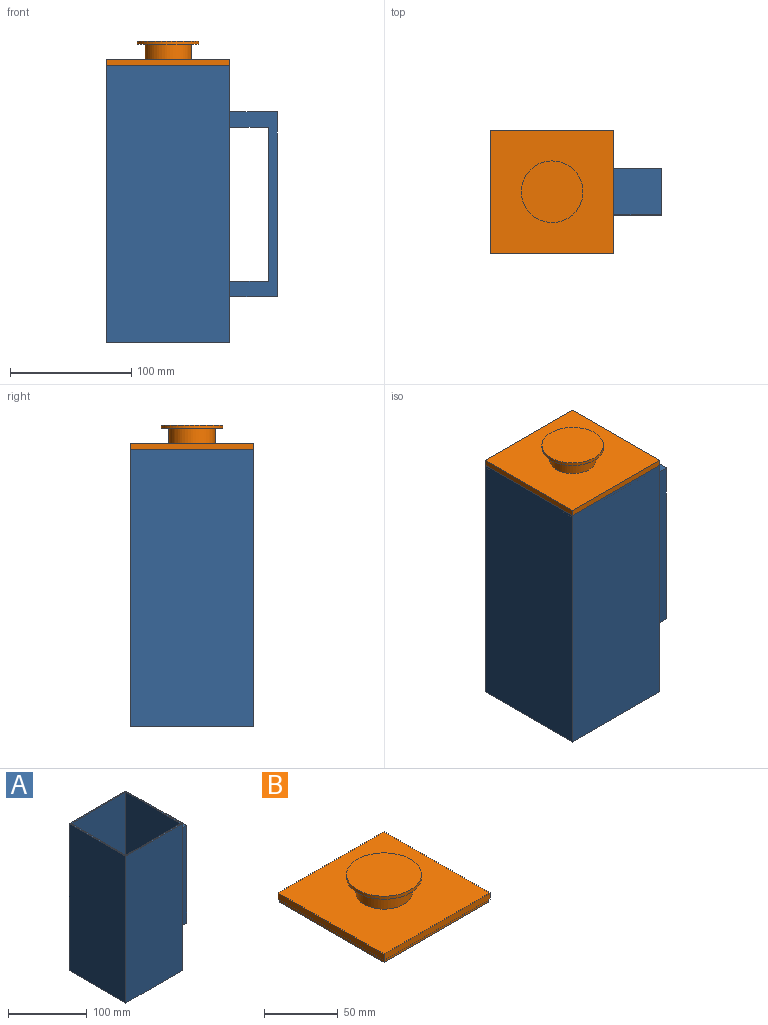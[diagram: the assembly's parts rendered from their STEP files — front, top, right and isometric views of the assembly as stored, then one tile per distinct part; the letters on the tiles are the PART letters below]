
ASSEMBLY  parts=2 mates=1
PART A: 19 faces, bbox 141x101.6x228.6 mm
  f0: plane 101.6x101.6mm, normal (0,0,1), area 635.1mm2, adj f1,f2,f3,f4,f14,f15,f16,f17
  f1: plane 228.6x101.6mm, normal (1,0,0), area 22258mm2, adj f0,f2,f4,f5,f6,f7,f8,f9
  f2: plane 228.6x101.6mm, normal (0,1,0), area 23225.8mm2, adj f0,f1,f3,f5
  f3: plane 228.6x101.6mm, normal (-1,0,0), area 23225.8mm2, adj f0,f2,f4,f5
  f4: plane 228.6x101.6mm, normal (0,-1,0), area 23225.8mm2, adj f0,f1,f3,f5
  f5: plane 101.6x101.6mm, normal (0,0,-1), area 10322.6mm2, adj f1,f2,f3,f4
  f6: plane 152.4x39.37mm, normal (0,1,0), area 1967.7mm2, adj f1,f7,f9,f10,f11,f12,f13
  f7: plane 39.37x38.1mm, normal (0,0,1), area 1500mm2, adj f1,f6,f8,f13
  f8: plane 152.4x39.37mm, normal (0,-1,0), area 1967.7mm2, adj f1,f7,f9,f10,f11,f12,f13
  f9: plane 38.1x31.75mm, normal (0,0,-1), area 1209.7mm2, adj f1,f6,f8,f12
  f10: plane 38.1x31.75mm, normal (0,0,1), area 1209.7mm2, adj f1,f6,f8,f12
  f11: plane 39.37x38.1mm, normal (0,0,-1), area 1500mm2, adj f1,f6,f8,f13
  f12: plane 127x38.1mm, normal (-1,0,0), area 4838.7mm2, adj f6,f8,f9,f10
  f13: plane 152.4x38.1mm, normal (1,0,0), area 5806.4mm2, adj f6,f7,f8,f11
  f14: plane 227.01x98.43mm, normal (0,-1,0), area 22343.7mm2, adj f0,f15,f17,f18
  f15: plane 227.01x98.43mm, normal (1,0,0), area 22343.7mm2, adj f0,f14,f16,f18
  f16: plane 227.01x98.43mm, normal (0,1,0), area 22343.7mm2, adj f0,f15,f17,f18
  f17: plane 227.01x98.43mm, normal (-1,0,0), area 22343.7mm2, adj f0,f14,f16,f18
  f18: plane 98.43x98.43mm, normal (0,0,1), area 9687.5mm2, adj f14,f15,f16,f17
PART B: 15 faces, bbox 101.6x101.6x22.9 mm
  f0: plane 100.01x2.54mm, normal (-1,0,0), area 254mm2, adj f1,f3,f4,f10
  f1: plane 100.01x2.54mm, normal (0,-1,0), area 254mm2, adj f0,f2,f4,f10
  f2: plane 100.01x2.54mm, normal (1,0,0), area 254mm2, adj f1,f3,f4,f10
  f3: plane 100.01x2.54mm, normal (0,1,0), area 254mm2, adj f0,f2,f4,f10
  f4: plane 100.01x100.01mm, normal (0,0,-1), area 10002.5mm2, adj f0,f1,f2,f3
  f5: plane 101.6x5.08mm, normal (0,1,0), area 516.1mm2, adj f6,f8,f9,f10
  f6: plane 101.6x5.08mm, normal (-1,0,0), area 516.1mm2, adj f5,f7,f9,f10
  f7: plane 101.6x5.08mm, normal (0,-1,0), area 516.1mm2, adj f6,f8,f9,f10
  f8: plane 101.6x5.08mm, normal (1,0,0), area 516.1mm2, adj f5,f7,f9,f10
  f9: plane 101.6x101.6mm, normal (0,0,1), area 9182.5mm2, adj f5,f6,f7,f8,f11
  f10: plane 101.6x101.6mm, normal (0,0,-1), area 320.1mm2, adj f0,f1,f2,f3,f5,f6,f7,f8
  f11: cylinder r=19.05mm len=38.1mm, axis (0,0,-1), area 1520.1mm2, adj f9,f14
  f12: cylinder r=25.4mm len=50.8mm, axis (0,0,-1), area 405.4mm2, adj f13,f14
  f13: plane 50.8x50.8mm, normal (0,0,1), area 2026.8mm2, adj f12
  f14: plane 50.8x50.8mm, normal (0,0,-1), area 886.7mm2, adj f11,f12
PLACE A t=(137.9,96.4,-27.98)mm
PLACE B t=(-89.91,46.4,198.08)mm
MATE planar A.f4 <-> B.f7  axis (0,-1,0) through (137.9,45.6,86.32)mm
